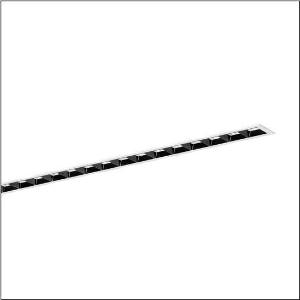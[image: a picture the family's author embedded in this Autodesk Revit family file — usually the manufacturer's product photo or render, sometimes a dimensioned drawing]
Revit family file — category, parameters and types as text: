
# Revit family: silica_r__21_51mx12dc3awb_9b9c
name_source: partatom
category: Lighting Fixtures
units: mm (PartAtom-declared; Revit-internal decimal feet)

## family parameters
Cut with Voids When Loaded = No
Host = Face
Light Source = No
Part Type = Normal
Room Calculation Point = No
Round Connector Dimension = Use Diameter
Shared = No

## types (1)
- --- (1 x LED, 10800 lm, 69.2 W, 3000K)
    Apparent Load = 69 VA
    CIE Flux Codes = 86 100 100 100 100
    Color Rendering = 80
    Color Temperature = 3000K
    Default Elevation = 1800 mm
    Description = Silica® 21, office luminaire, primary light control with darklight reflector, of PMMA, black, CAT 2 (L<= 3000cd/m²), light emission: direct distribution, primary light characteristic: symmetric, installation type: recessed, LED, rated luminous flux: 10.800lm, luminous efficacy: 156lm/W, light colour: 830, colour temperature: 3000K, with terminal, 3+2-pole, max. 2.5mm², mains connection: 220..240V, AC, 50/60Hz, rated input power: 69.2W, luminaire housing, of aluminium, traffic white (RAL 9016), length: 3.028mm, width: 79mm, height: 53mm, protection rating (complete): IP20, insulation class (complete): insulation class I (protective earthing), certification: CE, permissible operating ambient temperature: 0..+35°C, standard: EN 50419, packaging unit: 1 piece
    Height = 0 mm  [stored 0 ft]
    Lamp = 1 x LED
    Lamp Light Flux = 10800 lm
    Lamp Power = 69.2 W
    Lamp count = 1
    Length = 3027 mm
    Luminous efficacy = 156 lm/W
    Manufacturer = Siteco
    ModVariant = No
    Model = 51MX12DC3AWB
    Mounting Place = Ceiling
    Mounting Type = Recessed
    Number of Poles = 1
    OnlyDefault = Yes
    Power Factor = 1
    Product Name = Silica® 21
    Product group = office luminaire | ceiling recessed
    ProductGroupID = 401
    Protection Class = Protection class I
    Protection Degree = IP 20
    RLX_Detail_Level = 1
    RLX_Emergency_Light_Flux = 0 lm
    RLX_Emergency_Type = 0
    RLX_Emergency_Type_DB = No
    RlxData = <blob elided: 62973 chars, md5=56029e65>
    Socket = socket
    Standby Power = 0 W
    System Light Flux = 10800 lm
    System Power = 69 W
    Type Comments = factory setting: luminous flux: 100 % | dim-lin: 254 | 392 mA
    Type Image = l_1297791.jpg
    URL = http://relux.com
    VarID = @adj_055535
    Voltage = 0 V
    Weight = 0.00 kg
    Width = 79 mm

note: [stored X ft] marks values corroborated as IEEE doubles in the binary element streams (Revit-internal decimal feet)

## geometry (parser evidence)
native form markers: Blend x4, Sweep x8
no freeform markers — native parametric forms only
